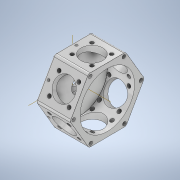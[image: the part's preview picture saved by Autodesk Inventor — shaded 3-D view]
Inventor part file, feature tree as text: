
AUTODESK INVENTOR PART (.ipt)
format: ipt  version: 2021.1 (Build 251245000, 245)  size: 485,888 bytes
history: native  units: in
note: dims shown in document units (in); Inventor stores cm internally (conversion verified against a paired STEP export)
features: thread x38, extrude x9, sketch x8, pattern_circular x4, chamfer x2, fillet x1
ambient origin geometry x8: Origin, YZ Plane, XZ Plane, XY Plane, X Axis, Y Axis, Z Axis, Center Point
bodies: Solid1 (feature_tree)
feature tree (62):
  extrude  "Extrusion1"  Depth=0.5in
  extrude  "Extrusion2"  Depth=4.5in
  chamfer  "Chamfer1"  Distance=4.5in
  extrude  "Extrusion3"  Depth=0.6in
  extrude  "Extrusion4"  Depth=1.2in TaperAngle=0.0deg
  pattern_circular  "Circular Pattern1"  Count=6 Angle=360.0deg
  thread  "Thread1"  [1 undecoded]
  thread  "Thread2"  [1 undecoded]
  thread  "Thread3"  [1 undecoded]
  thread  "Thread4"  [1 undecoded]
  thread  "Thread5"  [1 undecoded]
  thread  "Thread6"  [1 undecoded]
  thread  "Thread7"  [1 undecoded]
  extrude  "Extrusion5"  TaperAngle=45.0deg  [1 undecoded]
  pattern_circular  "Circular Pattern2"  [2 undecoded]
  thread  "Thread8"  [1 undecoded]
  thread  "Thread9"  [1 undecoded]
  thread  "Thread10"  [1 undecoded]
  thread  "Thread11"  [1 undecoded]
  thread  "Thread12"  [1 undecoded]
  thread  "Thread13"  [1 undecoded]
  thread  "Thread14"  [1 undecoded]
  thread  "Thread15"  [1 undecoded]
  thread  "Thread16"  [1 undecoded]
  thread  "Thread17"  [1 undecoded]
  thread  "Thread18"  [1 undecoded]
  thread  "Thread19"  [1 undecoded]
  thread  "Thread20"  [1 undecoded]
  thread  "Thread21"  [1 undecoded]
  thread  "Thread22"  [1 undecoded]
  thread  "Thread23"  [1 undecoded]
  thread  "Thread24"  [1 undecoded]
  thread  "Thread25"  [1 undecoded]
  thread  "Thread26"  [1 undecoded]
  thread  "Thread27"  [1 undecoded]
  thread  "Thread28"  [1 undecoded]
  thread  "Thread29"  [1 undecoded]
  thread  "Thread30"  [1 undecoded]
  thread  "Thread31"  [1 undecoded]
  thread  "Thread32"  [1 undecoded]
  thread  "Thread33"  [1 undecoded]
  thread  "Thread34"  [1 undecoded]
  thread  "Thread35"  [1 undecoded]
  thread  "Thread36"  [1 undecoded]
  thread  "Thread37"  [1 undecoded]
  thread  "Thread38"  [1 undecoded]
  fillet  "Fillet1"  Radius=1.233in
  sketch  "Sketch9"  dims[d18=2.5in]
  extrude  "Extrusion6"  Depth=0.8in TaperAngle=0.0deg
  extrude  "Extrusion7"  Depth=0.8in TaperAngle=0.0deg
  extrude  "Extrusion8"  Depth=0.2in
  pattern_circular  "Circular Pattern3"  [2 undecoded]
  extrude  "Extrusion9"  Depth=0.8in
  pattern_circular  "Circular Pattern4"  [2 undecoded]
  chamfer  "Chamfer2"  [1 undecoded]
  sketch  "Sketch1"  dims[d0=10.6in d1=0.5in]
  sketch  "Sketch2"  dims[d2=5.7in d3=0.0in d4=9.0in d5=4.5in d6=0.0in]
  sketch  "Sketch6"  dims[d7=0.02in d8=0.125in d9=45.0deg d10=0.6in]
  sketch  "Sketch7"  dims[d11=2.3622in d13=360.0deg d15=1.2in d16=0.0in]
  sketch  "Sketch8"  dims[d17=3.6in]
  sketch  "Sketch10"  dims[d19=1.2in d20=0.0in d21=2.3622in d22=360.0deg d24=1.2in d25=0.0in d26=1.2in d27=0.0in d28=1.2in d29=0.0in d30=1.2in d31=0.0in d32=1.2in d33=0.0in d34=1.2in d35=0.0in d36=1.2in d37=0.0in]
  sketch  "Sketch11"  dims[d38=4.6in d39=45.0deg d40=0.6in d41=1.5748in d43=360.0deg d45=1.2in d46=0.0in d47=2.3622in d48=360.0deg d50=1.233in d51=0.0in d52=1.233in d53=0.0in d54=1.233in d55=0.0in d56=1.233in d57=0.0in d58=1.233in d59=0.0in d60=1.233in d61=0.0in d62=1.233in d63=0.0in d64=1.233in d65=0.0in d66=1.233in d67=0.0in d68=1.233in d69=0.0in d70=1.233in d71=0.0in d72=1.233in d73=0.0in d74=1.233in d75=0.0in d76=1.233in d77=0.0in d78=1.233in d79=0.0in d80=1.233in d81=0.0in d82=1.233in d83=0.0in d84=1.233in d85=0.0in d86=1.233in d87=0.0in d88=1.233in d89=0.0in d90=1.233in d91=0.0in d92=1.233in d93=0.0in d94=1.233in d95=0.0in d96=1.233in d97=0.0in d98=1.233in d99=0.0in d100=1.233in d101=0.0in d102=1.233in d103=0.0in d104=10.6in d105=0.0in d106=1.233in d107=0.0in d108=1.233in d109=0.0in d110=1.233in d111=0.0in d112=0.2in d113=2.8in d114=1.4in d115=0.8in d116=0.0in d117=0.0in d118=0.0in d119=0.4in d120=3.6in d121=0.0in d122=2.3622in d123=360.0deg d125=0.4in d126=2.0in d127=0.8in d128=0.0in d129=2.3622in d130=360.0deg d132=0.01in d133=0.125in d134=45.0deg]
note: 46 required parameter values undecoded (feature->parameter linkage not recoverable at this tier; creation-order binding heuristic only, values carry confidence <= 0.55)
